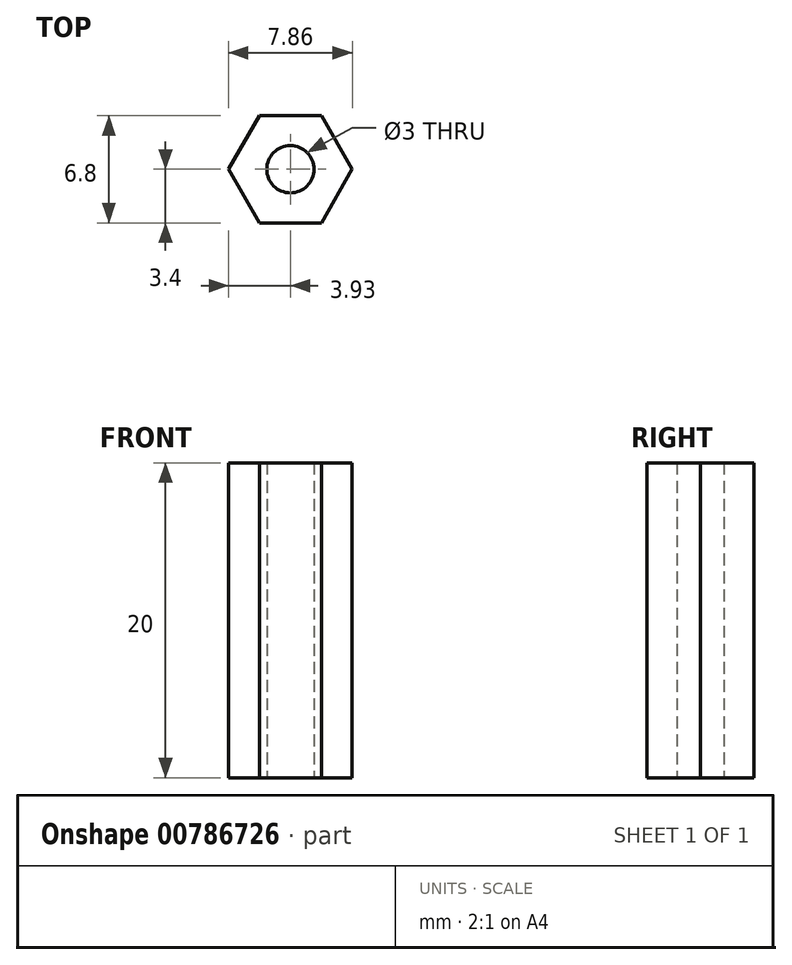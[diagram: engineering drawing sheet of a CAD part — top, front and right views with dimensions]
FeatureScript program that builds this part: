
annotation { "Feature Type Name" : "Feature", "Feature Type Description" : "" }
export const myFeature = defineFeature(function(context is Context, id is Id, definition is map)
    precondition{}
    {
        {
            var Q0;
            Q0=qCreatedBy(makeId("Top.planeOp"),FACE);
            var sketch = newSketch(context, id + "F0", { "sketchPlane" : qUnion([Q0])});
            skCircle(sketch, "E0", {"center": v(0, 0) * mm, "radius": 1.5 * mm});
            skCircle(sketch, "E1.cCircle", {"center": v(0, 0) * mm, "radius": 3.4 * mm, "construction": true});
            skLineSegment(sketch, "E1.0", {"start": v(1.96, -3.4) * mm, "end": v(-1.96, -3.4) * mm});
            skLineSegment(sketch, "E1.1", {"start": v(-1.96, -3.4) * mm, "end": v(-3.93, 0) * mm});
            skLineSegment(sketch, "E1.2", {"start": v(-3.93, 0) * mm, "end": v(-1.96, 3.4) * mm});
            skLineSegment(sketch, "E1.3", {"start": v(-1.96, 3.4) * mm, "end": v(1.96, 3.4) * mm});
            skLineSegment(sketch, "E1.4", {"start": v(1.96, 3.4) * mm, "end": v(3.93, 0) * mm});
            skLineSegment(sketch, "E1.5", {"start": v(3.93, 0) * mm, "end": v(1.96, -3.4) * mm});
            skPoint(sketch, "E1.0.midPoint", {"position": v(0, -3.4) * mm});
            skSolve(sketch);
        }
        {
            var Q0;
            Q0=makeQuery(id+"F0.imprint","IMPRINT",FACE,{"disambiguationData":[TD([[makeQuery(id+"F0.imprint","IMPRINT",EDGE,{"derivedFrom":sQuery(id+"F0.wireOp",EDGE,"E0")}),-1.0]])]});
            extrude(context, id + "F1", {"entities" : qUnion([Q0]), "depth" : 20 * mm, "offsetDistance" : 25 * mm});
        }
    });
